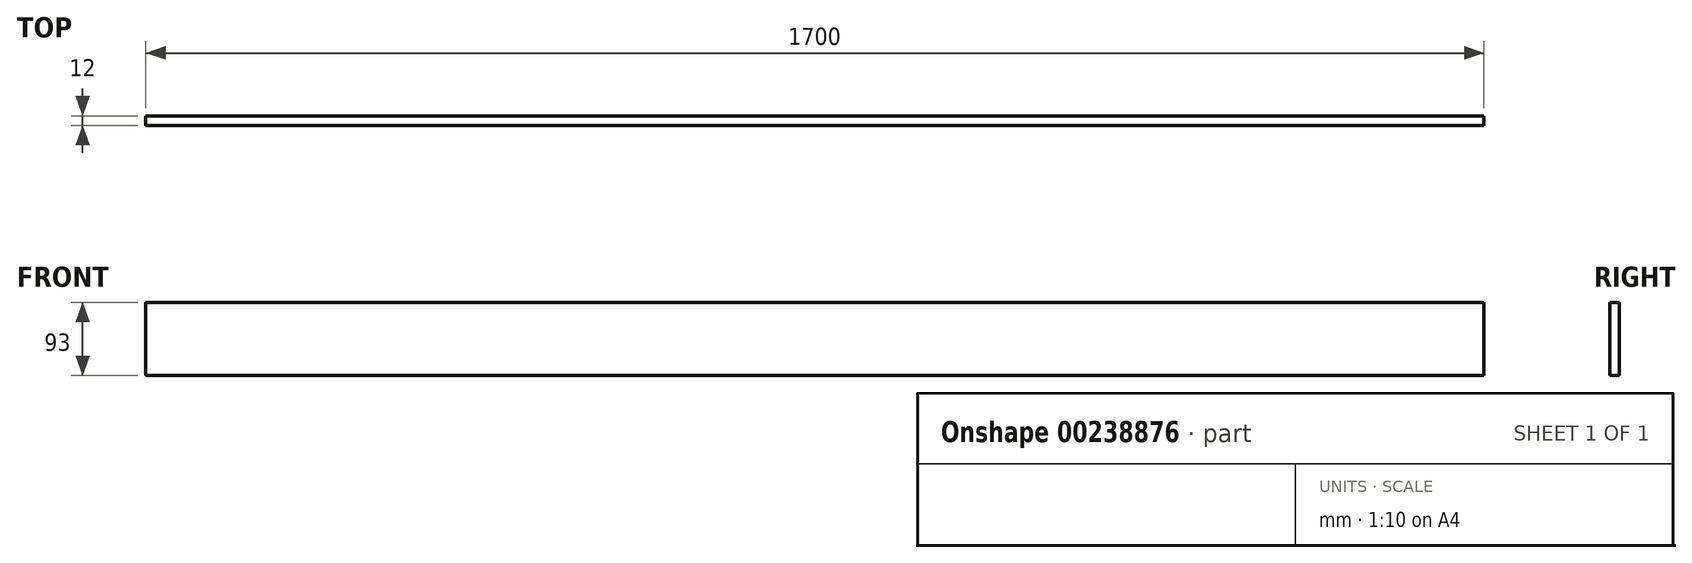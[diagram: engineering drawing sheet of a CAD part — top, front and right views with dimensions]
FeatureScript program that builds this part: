
annotation { "Feature Type Name" : "Feature", "Feature Type Description" : "" }
export const myFeature = defineFeature(function(context is Context, id is Id, definition is map)
    precondition{}
    {
        {
            var Q0;
            Q0=qCreatedBy(makeId("Front.planeOp"),FACE);
            var sketch = newSketch(context, id + "F0", { "sketchPlane" : qUnion([Q0])});
            skLineSegment(sketch, "E0.bottom", {"start": v(0, 0) * mm, "end": v(1700, 0) * mm});
            skLineSegment(sketch, "E0.top", {"start": v(0, 93) * mm, "end": v(1700, 93) * mm});
            skLineSegment(sketch, "E0.left", {"start": v(0, 0) * mm, "end": v(0, 93) * mm});
            skLineSegment(sketch, "E0.right", {"start": v(1700, 0) * mm, "end": v(1700, 93) * mm});
            skSolve(sketch);
        }
        {
            var Q0;
            Q0 = qSketchRegion(id + "F0", true);
            extrude(context, id + "F1", {"entities" : qUnion([Q0]), "offsetDistance" : 25 * mm, "depth" : 12 * mm});
        }
    });
